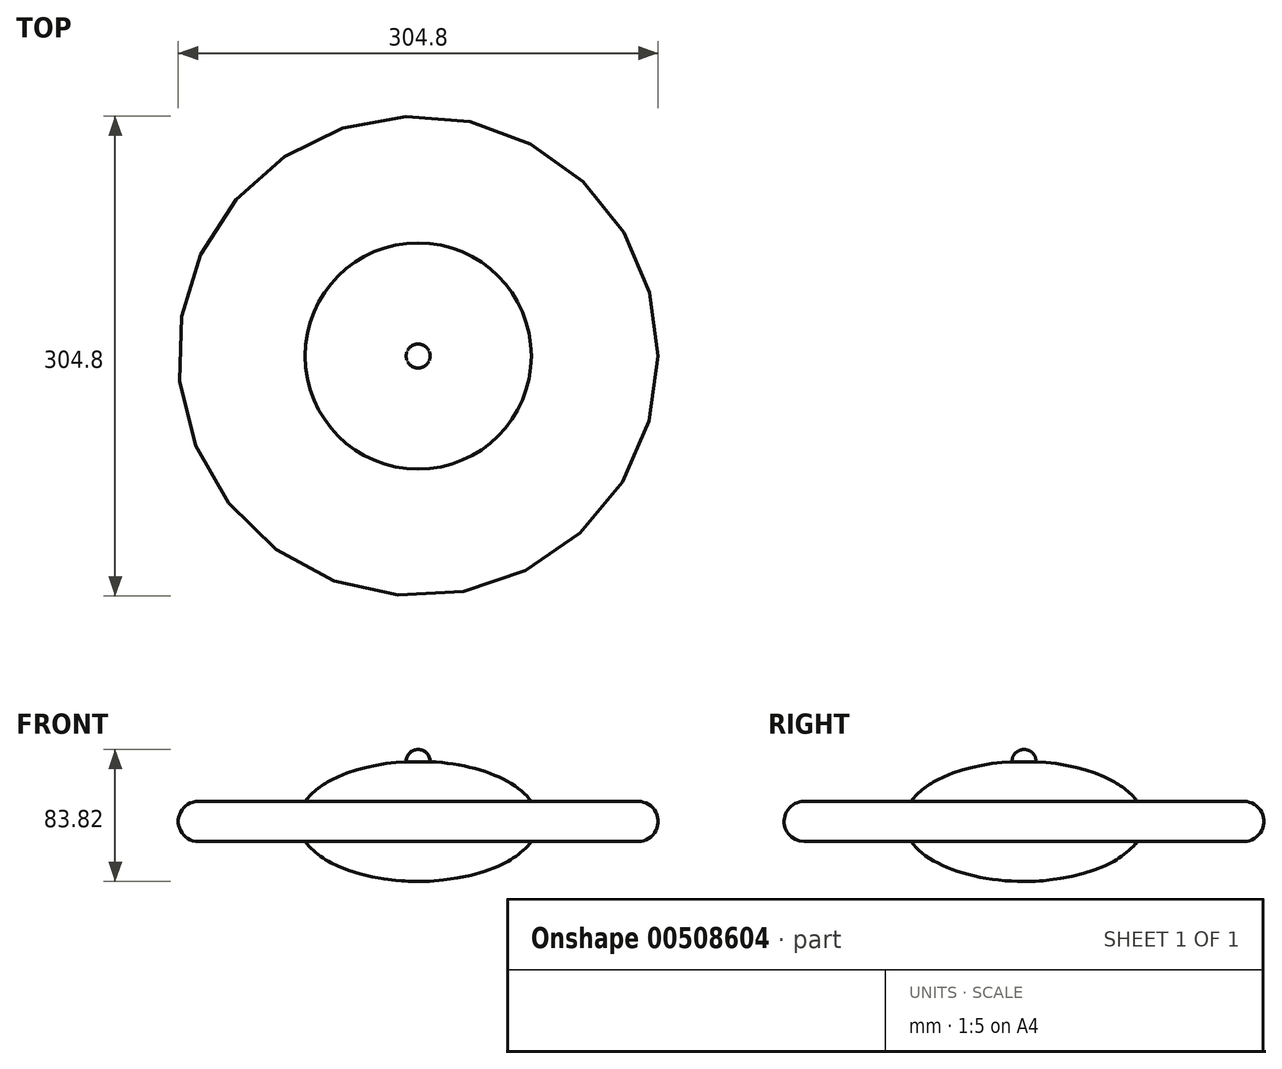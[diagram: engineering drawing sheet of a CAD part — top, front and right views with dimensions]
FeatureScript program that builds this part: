
annotation { "Feature Type Name" : "Feature", "Feature Type Description" : "" }
export const myFeature = defineFeature(function(context is Context, id is Id, definition is map)
    precondition{}
    {
        {
            var Q0;
            Q0=qCreatedBy(makeId("Right.planeOp"),FACE);
            var sketch = newSketch(context, id + "F0", { "sketchPlane" : qUnion([Q0])});
            skLineSegment(sketch, "E0.bottom", {"start": v(0, 12.7) * mm, "end": v(-152.4, 12.7) * mm});
            skLineSegment(sketch, "E0.top", {"start": v(0, -12.7) * mm, "end": v(-152.4, -12.7) * mm});
            skLineSegment(sketch, "E0.left", {"start": v(0, 12.7) * mm, "end": v(0, -12.7) * mm});
            skLineSegment(sketch, "E0.right", {"start": v(-152.4, 12.7) * mm, "end": v(-152.4, -12.7) * mm});
            skPoint(sketch, "E0.middle", {"position": v(-76.2, 0) * mm});
            skLineSegment(sketch, "E1", {"start": v(0, 84.1) * mm, "end": v(0, -132.4) * mm, "construction": true});
            skPoint(sketch, "E2", {"position": v(0, 0) * mm});
            skPoint(sketch, "E3", {"position": v(0, 9.81) * mm});
            skSolve(sketch);
        }
        {
            var Q0;
            Q0=makeQuery(id+"F0.imprint","IMPRINT",FACE,{"disambiguationData":[TD([[makeQuery(id+"F0.imprint","IMPRINT",EDGE,{"derivedFrom":sQuery(id+"F0.wireOp",EDGE,"E0.bottom")}),1.0]])]});
            var Q1;
            Q1=sQuery(id+"F0.wireOp",EDGE,"E1");
            revolve(context, id + "F1", {"entities" : qUnion([Q0]), "axis" : qUnion([Q1]), "revolveType" : RevolveType.FULL});
        }
        {
            var Q0;
            Q0=makeQuery(id+"F1.opRevolve","SWEPT_EDGE",EDGE,{"disambiguationData":[OSD([sQuery(id+"F0.wireOp",EDGE,"E0.bottom"),sQuery(id+"F0.wireOp",EDGE,"E0.right")])]});
            var Q1;
            Q1=makeQuery(id+"F1.opRevolve","SWEPT_EDGE",EDGE,{"disambiguationData":[OSD([sQuery(id+"F0.wireOp",EDGE,"E0.top"),sQuery(id+"F0.wireOp",EDGE,"E0.right")])]});
            fillet(context, id + "F2", {"entities" : qUnion([Q0, Q1]), "radius" : 12.7 * mm, "tangentPropagation" : true, "allowEdgeOverflow" : false});
        }
        {
            var Q0;
            Q0=qCreatedBy(makeId("Right.planeOp"),FACE);
            var sketch = newSketch(context, id + "F3", { "sketchPlane" : qUnion([Q0])});
            skEllipticalArc(sketch, "E4", {});
            skLineSegment(sketch, "E5", {"start": v(0, 38.1) * mm, "end": v(0, -38.1) * mm});
            const initialGuessF3  = {"E4": [0, 0, 1, 0, 0.0762, 0.0381, 1.5707963267948966, 4.71238898038469]};
            skSetInitialGuess(sketch, initialGuessF3);
            skSolve(sketch);
        }
        {
            var Q0;
            Q0 = qSketchRegion(id + "F3", true);
            var Q1;
            Q1=sQuery(id+"F3.wireOp",EDGE,"E5");
            revolve(context, id + "F4", {"operationType" : NewBodyOperationType.ADD, "entities" : qUnion([Q0]), "axis" : qUnion([Q1]), "revolveType" : RevolveType.FULL});
        }
        {
            var Q0;
            Q0=qCreatedBy(makeId("Top.planeOp"),FACE);
            cPlane(context, id + "F5", {"entities" : qUnion([Q0]), "cplaneType" : CPlaneType.OFFSET, "offset" : 38.1 * mm, "width" : 152.4 * mm, "height" : 152.4 * mm});
        }
        {
            var Q0;
            Q0=qCreatedBy(id+"F5.planeOp",FACE);
            var sketch = newSketch(context, id + "F6", { "sketchPlane" : qUnion([Q0])});
            skArc(sketch, "E6", {"start": v(7.62, 0) * mm, "mid": v(0, 7.62) * mm, "end": v(-7.62, 0) * mm});
            skLineSegment(sketch, "E7", {"start": v(-7.62, 0) * mm, "end": v(7.62, 0) * mm});
            skSolve(sketch);
        }
        {
            var Q0;
            Q0 = qSketchRegion(id + "F6", true);
            var Q1;
            Q1=sQuery(id+"F6.wireOp",EDGE,"E7");
            revolve(context, id + "F7", {"operationType" : NewBodyOperationType.ADD, "entities" : qUnion([Q0]), "axis" : qUnion([Q1]), "revolveType" : RevolveType.FULL});
        }
    });
